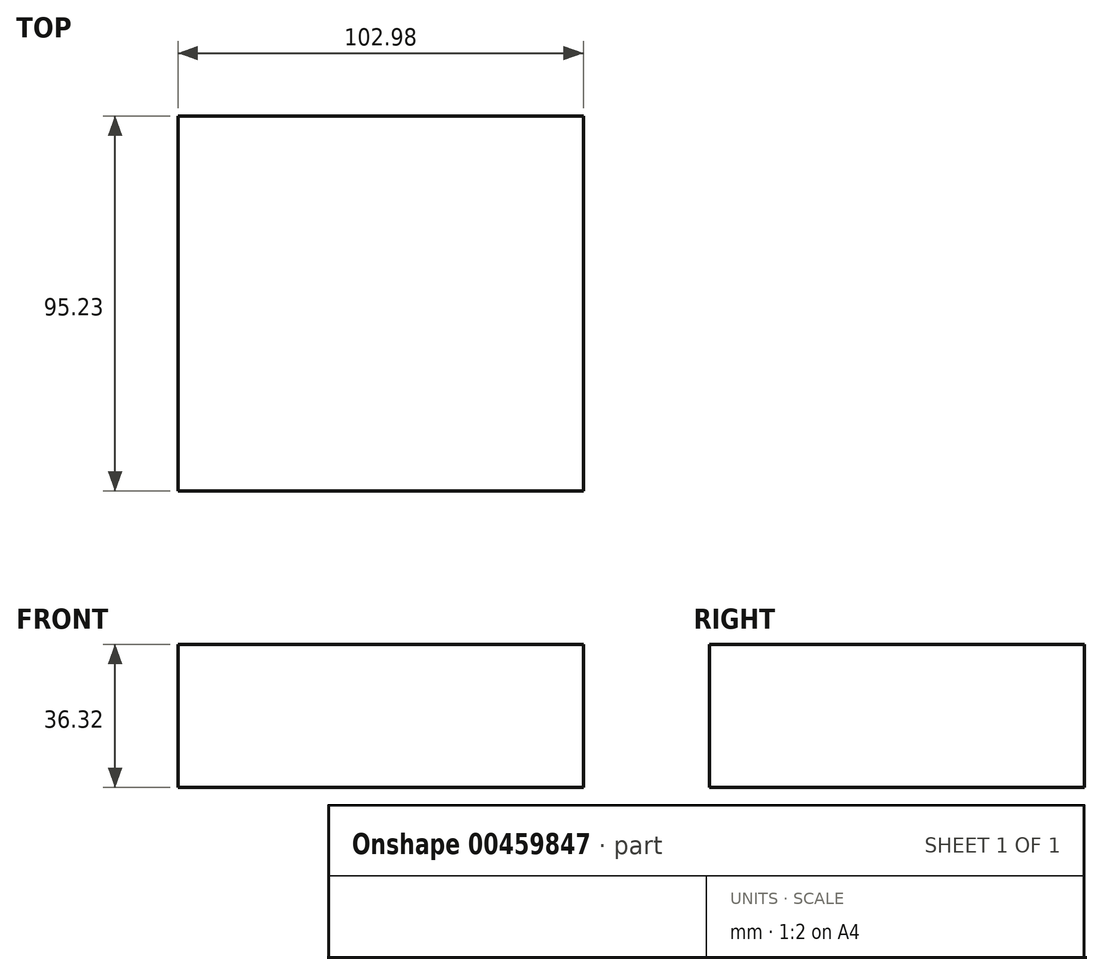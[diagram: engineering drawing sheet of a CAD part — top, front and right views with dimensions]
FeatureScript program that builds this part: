
annotation { "Feature Type Name" : "Feature", "Feature Type Description" : "" }
export const myFeature = defineFeature(function(context is Context, id is Id, definition is map)
    precondition{}
    {
        {
            var Q0;
            Q0=qCreatedBy(makeId("Top.planeOp"),FACE);
            var sketch = newSketch(context, id + "F0", { "sketchPlane" : qUnion([Q0])});
            skLineSegment(sketch, "E0.bottom", {"start": v(-52.63, -44.33) * mm, "end": v(50.35, -44.33) * mm});
            skLineSegment(sketch, "E0.top", {"start": v(-52.63, 50.9) * mm, "end": v(50.35, 50.9) * mm});
            skLineSegment(sketch, "E0.left", {"start": v(-52.63, -44.33) * mm, "end": v(-52.63, 50.9) * mm});
            skLineSegment(sketch, "E0.right", {"start": v(50.35, -44.33) * mm, "end": v(50.35, 50.9) * mm});
            skSolve(sketch);
        }
        {
            var Q0;
            Q0=makeQuery(id+"F0.imprint","IMPRINT",FACE,{"disambiguationData":[TD([[makeQuery(id+"F0.imprint","IMPRINT",EDGE,{"derivedFrom":sQuery(id+"F0.wireOp",EDGE,"E0.bottom")}),1.0]])]});
            extrude(context, id + "F1", {"entities" : qUnion([Q0]), "depth" : 36.32 * mm});
        }
    });
